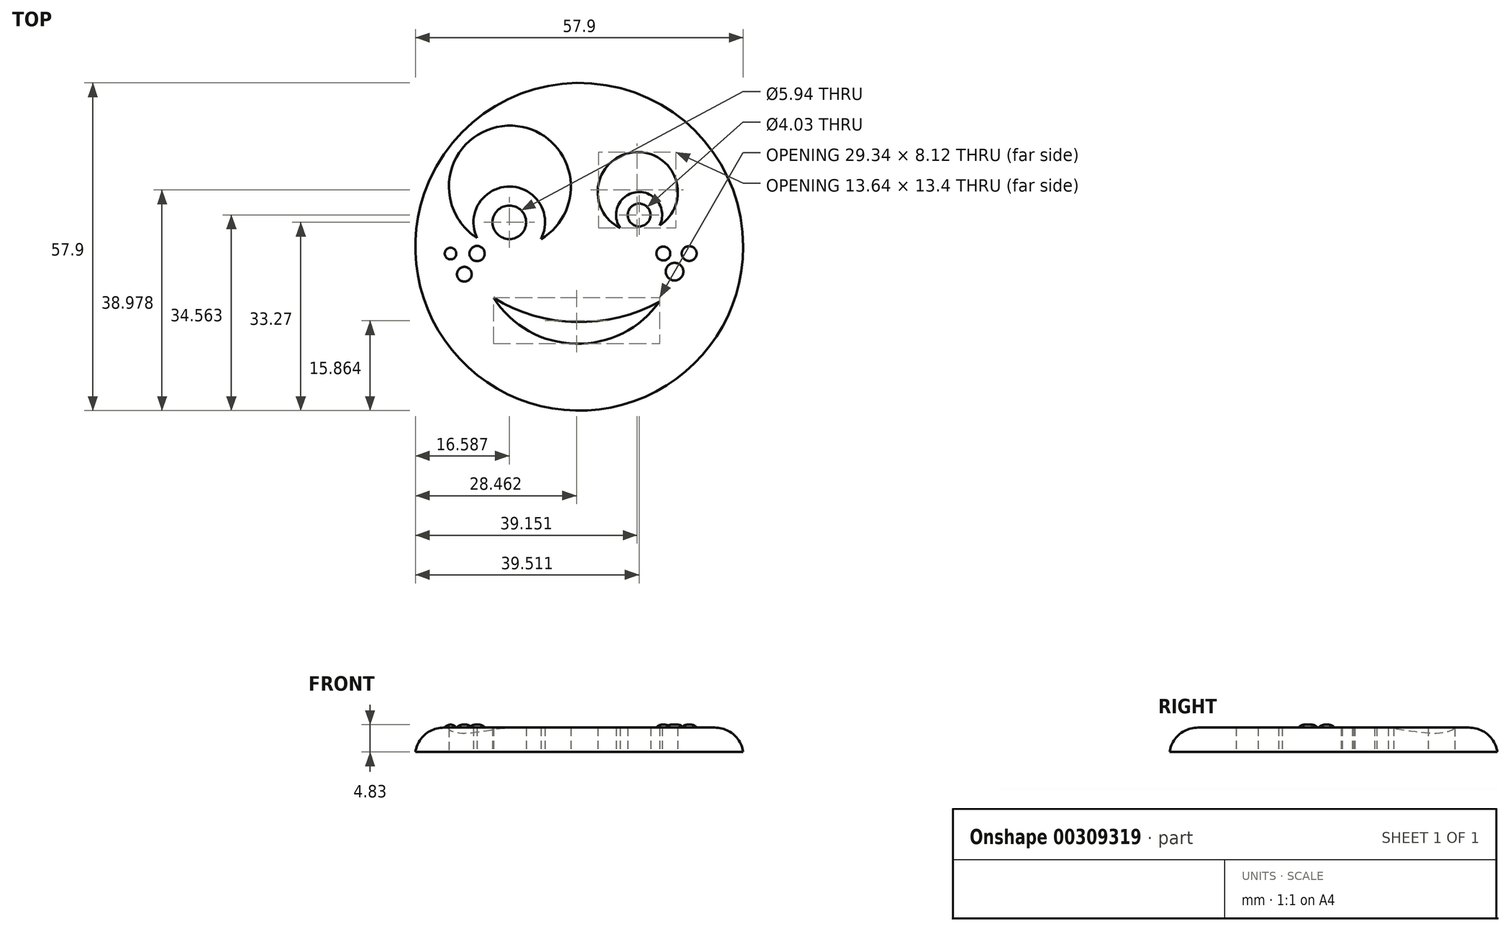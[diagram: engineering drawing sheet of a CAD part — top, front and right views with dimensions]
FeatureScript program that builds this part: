
annotation { "Feature Type Name" : "Feature", "Feature Type Description" : "" }
export const myFeature = defineFeature(function(context is Context, id is Id, definition is map)
    precondition{}
    {
        {
            var Q0;
            Q0=qCreatedBy(makeId("Top.planeOp"),FACE);
            var sketch = newSketch(context, id + "F0", { "sketchPlane" : qUnion([Q0])});
            skCircle(sketch, "E0", {"center": v(-40.87, 34.7) * mm, "radius": 28.95 * mm});
            skArc(sketch, "E1", {"start": v(-47.65, 36.06) * mm, "mid": v(-52.94, 56.11) * mm, "end": v(-58.92, 36.26) * mm});
            skArc(sketch, "E2", {"start": v(-26.69, 38.46) * mm, "mid": v(-31, 51.43) * mm, "end": v(-33.67, 38.03) * mm});
            skArc(sketch, "E3", {"start": v(-56.03, 25.68) * mm, "mid": v(-41.53, 17.55) * mm, "end": v(-26.69, 25.03) * mm});
            skArc(sketch, "E4", {"start": v(-56.03, 25.68) * mm, "mid": v(-41.44, 21.4) * mm, "end": v(-26.69, 25.03) * mm});
            skArc(sketch, "E5", {"start": v(-47.65, 36.06) * mm, "mid": v(-53.12, 45.34) * mm, "end": v(-58.92, 36.26) * mm});
            skArc(sketch, "E6", {"start": v(-26.69, 38.46) * mm, "mid": v(-30.56, 44.37) * mm, "end": v(-33.67, 38.03) * mm});
            skCircle(sketch, "E7", {"center": v(-53.23, 39.02) * mm, "radius": 2.97 * mm});
            skCircle(sketch, "E8", {"center": v(-30.3, 40.31) * mm, "radius": 2.01 * mm});
            skSolve(sketch);
        }
        {
            var Q0;
            Q0=makeQuery(id+"F0.imprint","IMPRINT",FACE,{"disambiguationData":[TD([[makeQuery(id+"F0.imprint","IMPRINT",EDGE,{"derivedFrom":sQuery(id+"F0.wireOp",EDGE,"E0")}),1.0]])]});
            extrude(context, id + "F1", {"entities" : qUnion([Q0]), "depth" : 4.32 * mm});
        }
        {
            var Q0;
            Q0=makeQuery(id+"F1.opExtrude","CAP_FACE",FACE,{"disambiguationData":[OSD([sQuery(id+"F0.wireOp",EDGE,"E0"),sQuery(id+"F0.wireOp",EDGE,"E1"),sQuery(id+"F0.wireOp",EDGE,"E2"),sQuery(id+"F0.wireOp",EDGE,"E3"),sQuery(id+"F0.wireOp",EDGE,"E4"),sQuery(id+"F0.wireOp",EDGE,"E5"),sQuery(id+"F0.wireOp",EDGE,"E6"),sQuery(id+"F0.wireOp",EDGE,"E7"),sQuery(id+"F0.wireOp",EDGE,"E8")])],"isStart":false});
            var sketch = newSketch(context, id + "F2", { "sketchPlane" : qUnion([Q0])});
            skCircle(sketch, "E9", {"center": v(-63.61, 33.5) * mm, "radius": 1.02 * mm});
            skCircle(sketch, "E10", {"center": v(-58.92, 33.5) * mm, "radius": 1.35 * mm});
            skCircle(sketch, "E11", {"center": v(-61.18, 29.85) * mm, "radius": 1.3 * mm});
            skCircle(sketch, "E12", {"center": v(-26.03, 33.5) * mm, "radius": 1.23 * mm});
            skCircle(sketch, "E13", {"center": v(-21.47, 33.5) * mm, "radius": 1.3 * mm});
            skCircle(sketch, "E14", {"center": v(-24.05, 30.3) * mm, "radius": 1.55 * mm});
            skSolve(sketch);
        }
        {
            var Q0;
            Q0 = qSketchRegion(id + "F2", true);
            extrude(context, id + "F3", {"entities" : qUnion([Q0]), "operationType" : NewBodyOperationType.ADD, "depth" : 0.5 * mm});
        }
        {
            var Q0;
            Q0=makeQuery(id+"F3.opExtrude","CAP_EDGE",EDGE,{"disambiguationData":[OSD([sQuery(id+"F2.wireOp",EDGE,"E9")])],"isStart":false});
            var Q1;
            Q1=makeQuery(id+"F3.opExtrude","CAP_EDGE",EDGE,{"disambiguationData":[OSD([sQuery(id+"F2.wireOp",EDGE,"E10")])],"isStart":false});
            var Q2;
            Q2=makeQuery(id+"F3.opExtrude","CAP_EDGE",EDGE,{"disambiguationData":[OSD([sQuery(id+"F2.wireOp",EDGE,"E11")])],"isStart":false});
            var Q3;
            Q3=makeQuery(id+"F3.opExtrude","CAP_EDGE",EDGE,{"disambiguationData":[OSD([sQuery(id+"F2.wireOp",EDGE,"E12")])],"isStart":false});
            var Q4;
            Q4=makeQuery(id+"F3.opExtrude","CAP_EDGE",EDGE,{"disambiguationData":[OSD([sQuery(id+"F2.wireOp",EDGE,"E13")])],"isStart":false});
            var Q5;
            Q5=makeQuery(id+"F3.opExtrude","CAP_EDGE",EDGE,{"disambiguationData":[OSD([sQuery(id+"F2.wireOp",EDGE,"E14")])],"isStart":false});
            fillet(context, id + "F4", {"entities" : qUnion([Q0, Q1, Q2, Q3, Q4, Q5]), "radius" : 1.17 * mm, "tangentPropagation" : true, "allowEdgeOverflow" : false});
        }
        {
            var Q0;
            Q0=makeQuery(id+"F1.opExtrude","CAP_EDGE",EDGE,{"disambiguationData":[OSD([sQuery(id+"F0.wireOp",EDGE,"E0")])],"isStart":false});
            fillet(context, id + "F5", {"entities" : qUnion([Q0]), "radius" : 5.08 * mm, "tangentPropagation" : true, "allowEdgeOverflow" : false});
        }
    });
